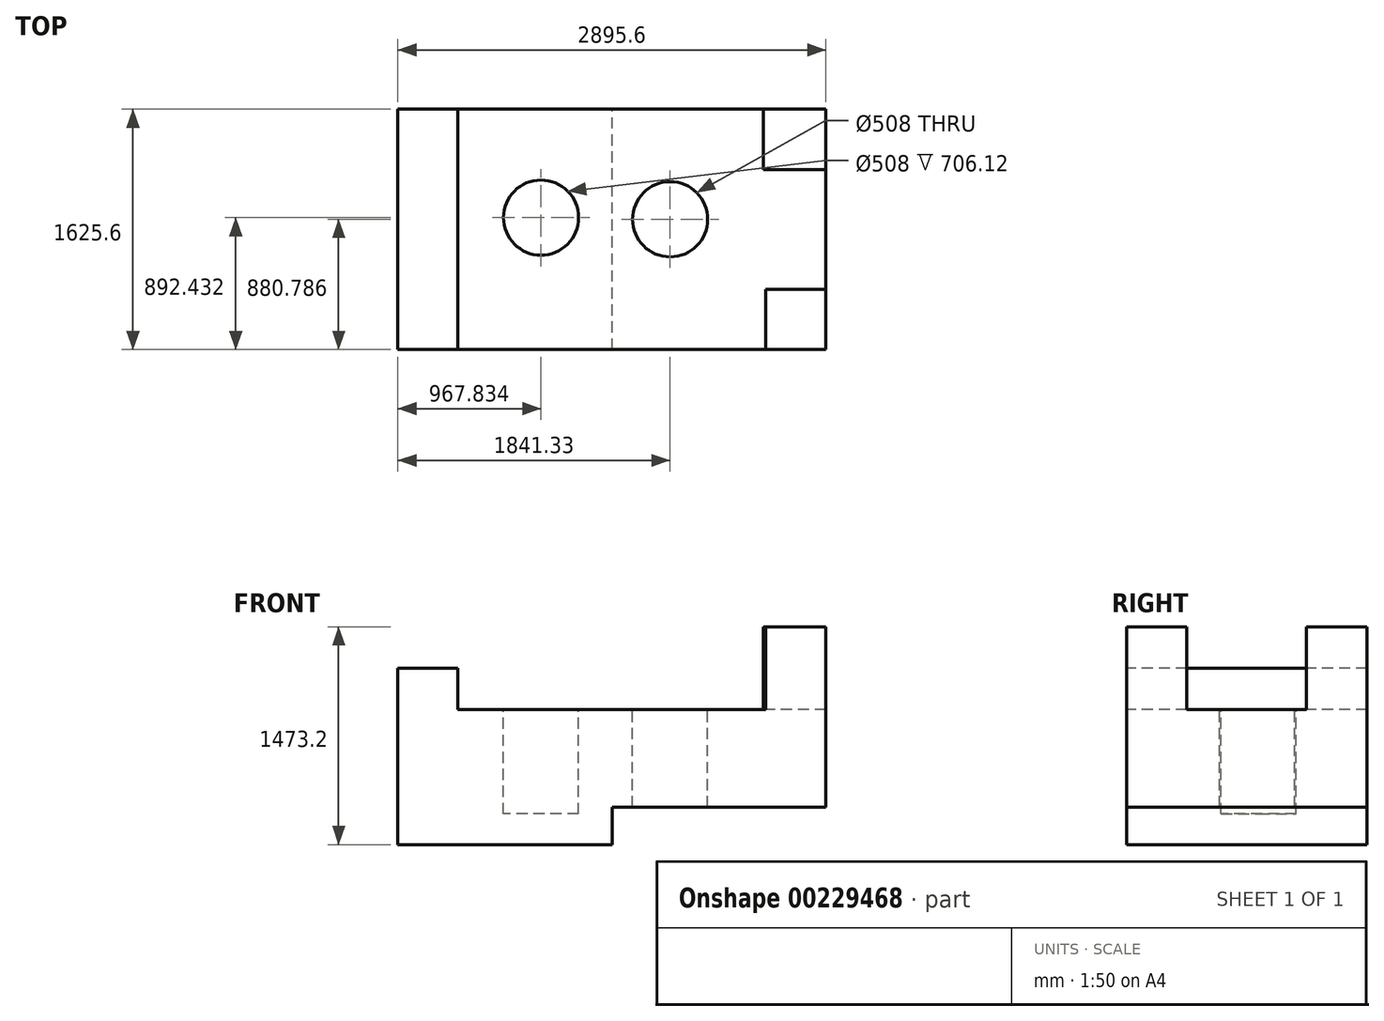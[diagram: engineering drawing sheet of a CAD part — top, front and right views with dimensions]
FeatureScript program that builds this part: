
annotation { "Feature Type Name" : "Feature", "Feature Type Description" : "" }
export const myFeature = defineFeature(function(context is Context, id is Id, definition is map)
    precondition{}
    {
        {
            var Q0;
            Q0=qCreatedBy(makeId("Top.planeOp"),FACE);
            var sketch = newSketch(context, id + "F0", { "sketchPlane" : qUnion([Q0])});
            skLineSegment(sketch, "E0.bottom", {"start": v(-1457.63, 718.77) * mm, "end": v(1437.97, 718.77) * mm});
            skLineSegment(sketch, "E0.top", {"start": v(-1457.63, -906.83) * mm, "end": v(1437.97, -906.83) * mm});
            skLineSegment(sketch, "E0.left", {"start": v(-1457.63, 718.77) * mm, "end": v(-1457.63, -906.83) * mm});
            skLineSegment(sketch, "E0.right", {"start": v(1437.97, 718.77) * mm, "end": v(1437.97, -906.83) * mm});
            skSolve(sketch);
        }
        {
            var Q0;
            Q0 = qSketchRegion(id + "F0", true);
            extrude(context, id + "F1", {"entities" : qUnion([Q0]), "depth" : 914.4 * mm});
        }
        {
            var Q0;
            Q0=makeQuery(id+"F0.imprint","IMPRINT",FACE,{"disambiguationData":[TD([[makeQuery(id+"F0.imprint","IMPRINT",EDGE,{"derivedFrom":sQuery(id+"F0.wireOp",EDGE,"E0.bottom")}),-1.0]])]});
            var sketch = newSketch(context, id + "F2", { "sketchPlane" : qUnion([Q0])});
            skLineSegment(sketch, "E1.bottom", {"start": v(1440.27, -909.78) * mm, "end": v(-7.53, -909.78) * mm});
            skLineSegment(sketch, "E1.top", {"start": v(1440.27, -503.38) * mm, "end": v(-7.53, -503.38) * mm});
            skLineSegment(sketch, "E1.left", {"start": v(1440.27, -909.78) * mm, "end": v(1440.27, -503.38) * mm});
            skLineSegment(sketch, "E1.right", {"start": v(-7.53, -909.78) * mm, "end": v(-7.53, -503.38) * mm});
            skSolve(sketch);
        }
        {
            var Q0;
            Q0 = qSketchRegion(id + "F2", true);
            extrude(context, id + "F3", {"entities" : qUnion([Q0]), "operationType" : NewBodyOperationType.REMOVE, "depth" : 254 * mm});
        }
        {
            var Q0;
            Q0=qCreatedBy(makeId("Top.planeOp"),FACE);
            var sketch = newSketch(context, id + "F4", { "sketchPlane" : qUnion([Q0])});
            skLineSegment(sketch, "E2", {"start": v(-7.73, -909.53) * mm, "end": v(-7.73, 720.65) * mm});
            skLineSegment(sketch, "E3", {"start": v(-7.73, 720.65) * mm, "end": v(1452.23, 720.65) * mm});
            skLineSegment(sketch, "E4", {"start": v(1452.23, 720.65) * mm, "end": v(1452.23, -902.34) * mm});
            skLineSegment(sketch, "E5", {"start": v(1452.23, -902.34) * mm, "end": v(-7.73, -909.53) * mm});
            skSolve(sketch);
        }
        {
            var Q0;
            Q0 = qSketchRegion(id + "F4", true);
            extrude(context, id + "F5", {"entities" : qUnion([Q0]), "operationType" : NewBodyOperationType.REMOVE, "depth" : 254 * mm});
        }
        {
            var Q0;
            Q0=makeQuery(id+"F1.opExtrude","CAP_FACE",FACE,{"disambiguationData":[OSD([sQuery(id+"F0.wireOp",EDGE,"E0.bottom"),sQuery(id+"F0.wireOp",EDGE,"E0.top"),sQuery(id+"F0.wireOp",EDGE,"E0.left"),sQuery(id+"F0.wireOp",EDGE,"E0.right")])],"isStart":false});
            var sketch = newSketch(context, id + "F6", { "sketchPlane" : qUnion([Q0])});
            skLineSegment(sketch, "E6.bottom", {"start": v(1437.97, -500.43) * mm, "end": v(1031.57, -500.43) * mm});
            skLineSegment(sketch, "E6.top", {"start": v(1437.97, -906.83) * mm, "end": v(1031.57, -906.83) * mm});
            skLineSegment(sketch, "E6.left", {"start": v(1437.97, -500.43) * mm, "end": v(1437.97, -906.83) * mm});
            skLineSegment(sketch, "E6.right", {"start": v(1031.57, -500.43) * mm, "end": v(1031.57, -906.83) * mm});
            skSolve(sketch);
        }
        {
            var Q0;
            Q0 = qSketchRegion(id + "F6", true);
            extrude(context, id + "F7", {"entities" : qUnion([Q0]), "operationType" : NewBodyOperationType.ADD, "depth" : 558.8 * mm});
        }
        {
            var Q0;
            Q0=makeQuery(id+"F1.opExtrude","CAP_FACE",FACE,{"disambiguationData":[OSD([sQuery(id+"F0.wireOp",EDGE,"E0.bottom"),sQuery(id+"F0.wireOp",EDGE,"E0.top"),sQuery(id+"F0.wireOp",EDGE,"E0.left"),sQuery(id+"F0.wireOp",EDGE,"E0.right")])],"isStart":false});
            var sketch = newSketch(context, id + "F8", { "sketchPlane" : qUnion([Q0])});
            skLineSegment(sketch, "E7.bottom", {"start": v(1437.97, 718.77) * mm, "end": v(1013.29, 718.77) * mm});
            skLineSegment(sketch, "E7.top", {"start": v(1437.97, 308.99) * mm, "end": v(1013.29, 308.99) * mm});
            skLineSegment(sketch, "E7.left", {"start": v(1437.97, 718.77) * mm, "end": v(1437.97, 308.99) * mm});
            skLineSegment(sketch, "E7.right", {"start": v(1013.29, 718.77) * mm, "end": v(1013.29, 308.99) * mm});
            skSolve(sketch);
        }
        {
            var Q0;
            Q0 = qSketchRegion(id + "F8", true);
            extrude(context, id + "F9", {"entities" : qUnion([Q0]), "operationType" : NewBodyOperationType.ADD, "depth" : 558.8 * mm});
        }
        {
            var Q0;
            Q0=makeQuery(id+"F1.opExtrude","CAP_FACE",FACE,{"disambiguationData":[OSD([sQuery(id+"F0.wireOp",EDGE,"E0.bottom"),sQuery(id+"F0.wireOp",EDGE,"E0.top"),sQuery(id+"F0.wireOp",EDGE,"E0.left"),sQuery(id+"F0.wireOp",EDGE,"E0.right")])],"isStart":false});
            var sketch = newSketch(context, id + "F10", { "sketchPlane" : qUnion([Q0])});
            skLineSegment(sketch, "E8.bottom", {"start": v(-1457.63, 718.77) * mm, "end": v(-1051.23, 718.77) * mm});
            skLineSegment(sketch, "E8.top", {"start": v(-1457.63, -906.83) * mm, "end": v(-1051.23, -906.83) * mm});
            skLineSegment(sketch, "E8.left", {"start": v(-1457.63, 718.77) * mm, "end": v(-1457.63, -906.83) * mm});
            skLineSegment(sketch, "E8.right", {"start": v(-1051.23, 718.77) * mm, "end": v(-1051.23, -906.83) * mm});
            skSolve(sketch);
        }
        {
            var Q0;
            Q0 = qSketchRegion(id + "F10", true);
            extrude(context, id + "F11", {"entities" : qUnion([Q0]), "operationType" : NewBodyOperationType.ADD, "depth" : 279.4 * mm});
        }
        {
            var Q0;
            Q0=makeQuery(id+"F1.opExtrude","CAP_FACE",FACE,{"disambiguationData":[OSD([sQuery(id+"F0.wireOp",EDGE,"E0.bottom"),sQuery(id+"F0.wireOp",EDGE,"E0.top"),sQuery(id+"F0.wireOp",EDGE,"E0.left"),sQuery(id+"F0.wireOp",EDGE,"E0.right")])],"isStart":false});
            var sketch = newSketch(context, id + "F12", { "sketchPlane" : qUnion([Q0])});
            skCircle(sketch, "E9", {"center": v(-489.8, -14.4) * mm, "radius": 254 * mm});
            skCircle(sketch, "E10", {"center": v(383.7, -26.04) * mm, "radius": 254 * mm});
            skSolve(sketch);
        }
        {
            var Q0;
            Q0 = qSketchRegion(id + "F12", true);
            extrude(context, id + "F13", {"entities" : qUnion([Q0]), "operationType" : NewBodyOperationType.REMOVE, "oppositeDirection" : true, "depth" : 706.12 * mm});
        }
    });
